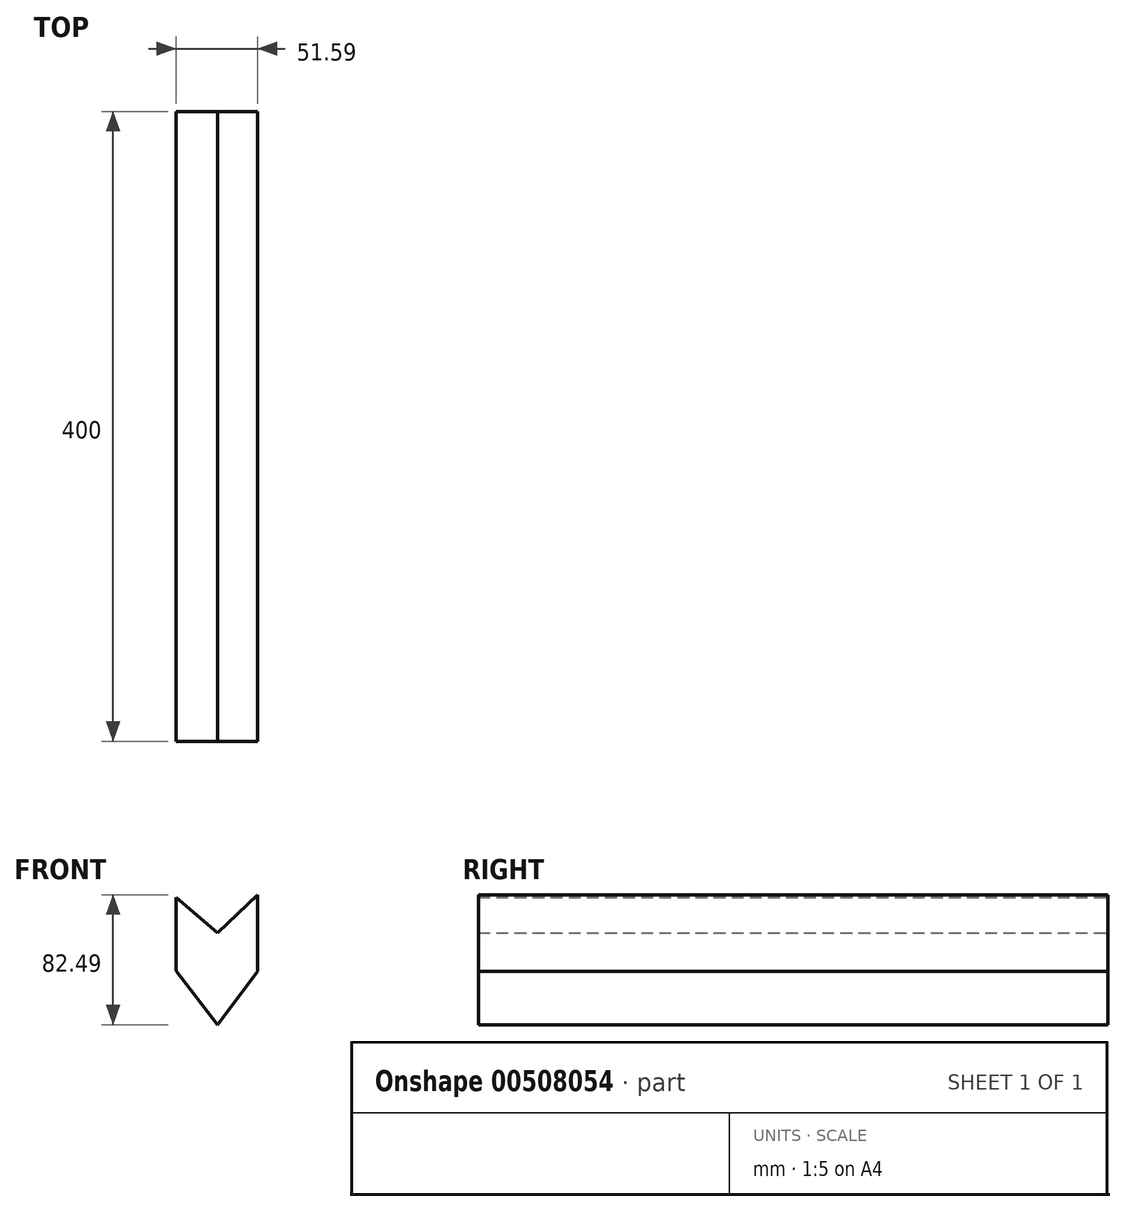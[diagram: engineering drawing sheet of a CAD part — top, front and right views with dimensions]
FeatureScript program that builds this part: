
annotation { "Feature Type Name" : "Feature", "Feature Type Description" : "" }
export const myFeature = defineFeature(function(context is Context, id is Id, definition is map)
    precondition{}
    {
        {
            var Q0;
            Q0=qCreatedBy(makeId("Front.planeOp"),FACE);
            var sketch = newSketch(context, id + "F0", { "sketchPlane" : qUnion([Q0])});
            skLineSegment(sketch, "E0", {"start": v(0, 28.13) * mm, "end": v(25.36, 52.32) * mm});
            skLineSegment(sketch, "E1", {"start": v(0, 28.13) * mm, "end": v(-26.23, 50.57) * mm});
            skLineSegment(sketch, "E2", {"start": v(-26.23, 50.57) * mm, "end": v(-26.23, 3.93) * mm});
            skLineSegment(sketch, "E3", {"start": v(25.36, 52.32) * mm, "end": v(25.36, 3.64) * mm});
            skLineSegment(sketch, "E4", {"start": v(25.36, 3.64) * mm, "end": v(0, -30.17) * mm});
            skLineSegment(sketch, "E5", {"start": v(0, -30.17) * mm, "end": v(-26.23, 3.93) * mm});
            skSolve(sketch);
        }
        {
            var Q0;
            Q0=makeQuery(id+"F0.imprint","IMPRINT",FACE,{"disambiguationData":[TD([[makeQuery(id+"F0.imprint","IMPRINT",EDGE,{"derivedFrom":sQuery(id+"F0.wireOp",EDGE,"E0")}),-1.0]])]});
            extrude(context, id + "F1", {"entities" : qUnion([Q0]), "endBound" : BoundingType.SYMMETRIC, "depth" : 400 * mm});
        }
    });
